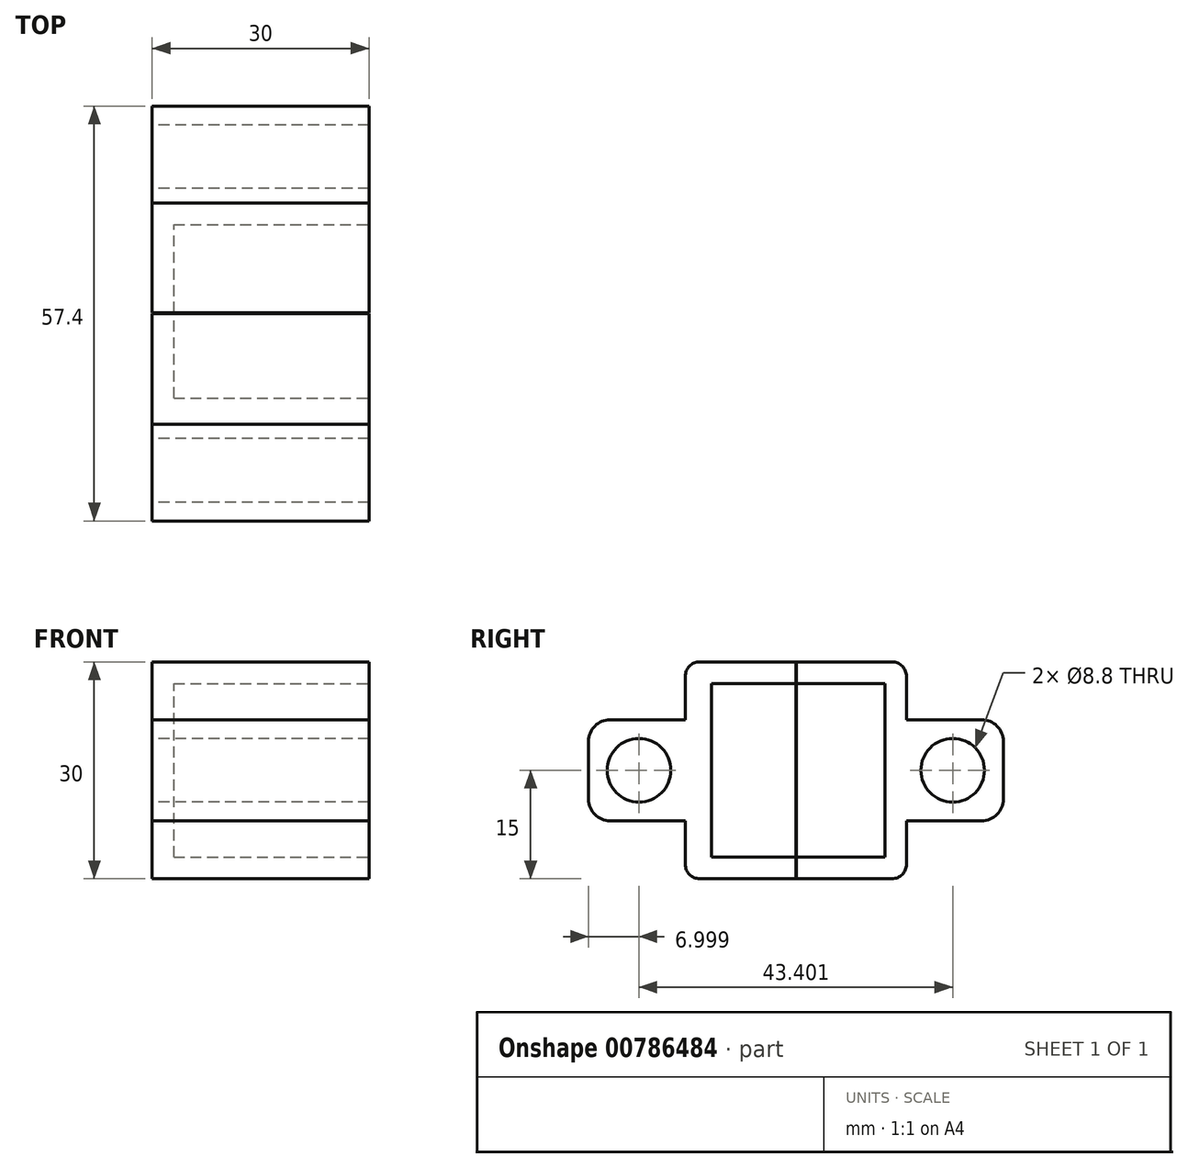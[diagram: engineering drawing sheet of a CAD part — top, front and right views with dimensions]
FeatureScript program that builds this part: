
annotation { "Feature Type Name" : "Feature", "Feature Type Description" : "" }
export const myFeature = defineFeature(function(context is Context, id is Id, definition is map)
    precondition{}
    {
        {
            var Q0;
            Q0=qCreatedBy(makeId("Top.planeOp"),FACE);
            var sketch = newSketch(context, id + "F0", { "sketchPlane" : qUnion([Q0])});
            skLineSegment(sketch, "E0.bottom", {"start": v(0, 15.3) * mm, "end": v(30, 15.3) * mm});
            skLineSegment(sketch, "E0.top", {"start": v(0, -14.7) * mm, "end": v(30, -14.7) * mm});
            skLineSegment(sketch, "E0.left", {"start": v(0, 15.3) * mm, "end": v(0, -14.7) * mm});
            skLineSegment(sketch, "E0.right", {"start": v(30, 15.3) * mm, "end": v(30, -14.7) * mm});
            skSolve(sketch);
        }
        {
            var Q0;
            Q0 = qSketchRegion(id + "F0", true);
            extrude(context, id + "F1", {"entities" : qUnion([Q0]), "depth" : 30 * mm, "offsetDistance" : 25 * mm});
        }
        {
            var Q0;
            Q0=makeQuery(id+"F1.opExtrude","SWEPT_FACE",FACE,{"disambiguationData":[OSD([sQuery(id+"F0.wireOp",EDGE,"E0.top")])]});
            var sketch = newSketch(context, id + "F2", { "sketchPlane" : qUnion([Q0])});
            skLineSegment(sketch, "E1.bottom", {"start": v(0, 8) * mm, "end": v(30, 8) * mm});
            skLineSegment(sketch, "E1.top", {"start": v(0, 22) * mm, "end": v(30, 22) * mm});
            skLineSegment(sketch, "E1.left", {"start": v(0, 8) * mm, "end": v(0, 22) * mm});
            skLineSegment(sketch, "E1.right", {"start": v(30, 8) * mm, "end": v(30, 22) * mm});
            skSolve(sketch);
        }
        {
            var Q0;
            Q0 = qSketchRegion(id + "F2", true);
            extrude(context, id + "F3", {"entities" : qUnion([Q0]), "operationType" : NewBodyOperationType.ADD, "depth" : 14 * mm, "offsetDistance" : 25 * mm});
        }
        {
            var Q0;
            Q0=makeQuery(id+"F3.boolean.opBoolean","MERGE",FACE,{"derivedFrom":[makeQuery(id+"F1.opExtrude","SWEPT_FACE",FACE,{"disambiguationData":[OSD([sQuery(id+"F0.wireOp",EDGE,"E0.left")])]}),makeQuery(id+"F3.opExtrude","SWEPT_FACE",FACE,{"disambiguationData":[OSD([sQuery(id+"F2.wireOp",EDGE,"E1.left")])]})]});
            var sketch = newSketch(context, id + "F4", { "sketchPlane" : qUnion([Q0])});
            skCircle(sketch, "E2", {"center": v(21.7, 15) * mm, "radius": 4.4 * mm});
            skPoint(sketch, "E2.centerSnap0", {"position": v(28.7, 15) * mm});
            skPoint(sketch, "E2.centerSnap1", {"position": v(21.7, 8) * mm});
            skSolve(sketch);
        }
        {
            var Q0;
            Q0 = qSketchRegion(id + "F4", true);
            extrude(context, id + "F5", {"entities" : qUnion([Q0]), "operationType" : NewBodyOperationType.REMOVE, "oppositeDirection" : true, "depth" : 30 * mm, "offsetDistance" : 25 * mm});
        }
        {
            var Q0;
            Q0=makeQuery(id+"F1.opExtrude","SWEPT_BODY",BODY,{"disambiguationData":[OSD([sQuery(id+"F0.wireOp",EDGE,"E0.bottom"),sQuery(id+"F0.wireOp",EDGE,"E0.top"),sQuery(id+"F0.wireOp",EDGE,"E0.left"),sQuery(id+"F0.wireOp",EDGE,"E0.right")])]});
            var Q1;
            Q1=qCreatedBy(makeId("Front.planeOp"),FACE);
            mirror(context, id + "F6", {"operationType" : NewBodyOperationType.ADD, "entities" : qUnion([Q0]), "mirrorPlane" : qUnion([Q1])});
        }
        {
            var Q0;
            Q0=makeQuery(id+"F3.opExtrude","CAP_EDGE",EDGE,{"disambiguationData":[OSD([sQuery(id+"F2.wireOp",EDGE,"E1.bottom")])],"isStart":false});
            var Q1;
            Q1=makeQuery(id+"F3.opExtrude","CAP_EDGE",EDGE,{"disambiguationData":[OSD([sQuery(id+"F2.wireOp",EDGE,"E1.top")])],"isStart":false});
            fillet(context, id + "F7", {"entities" : qUnion([Q0, Q1]), "radius" : 3 * mm, "tangentPropagation" : true, "allowEdgeOverflow" : false});
        }
        {
            var Q0;
            Q0=makeQuery(id+"F6.opPattern","COPY",EDGE,{"derivedFrom":makeQuery(id+"F3.opExtrude","CAP_EDGE",EDGE,{"disambiguationData":[OSD([sQuery(id+"F2.wireOp",EDGE,"E1.bottom")])],"isStart":false}),"instanceName":"1"});
            var Q1;
            Q1=makeQuery(id+"F6.opPattern","COPY",EDGE,{"derivedFrom":makeQuery(id+"F3.opExtrude","CAP_EDGE",EDGE,{"disambiguationData":[OSD([sQuery(id+"F2.wireOp",EDGE,"E1.top")])],"isStart":false}),"instanceName":"1"});
            fillet(context, id + "F8", {"entities" : qUnion([Q0, Q1]), "radius" : 3 * mm, "tangentPropagation" : true, "allowEdgeOverflow" : false});
        }
        {
            var Q0;
            {var subQ0=makeQuery(id+"F3.boolean.opBoolean","MERGE",FACE,{"derivedFrom":[makeQuery(id+"F1.opExtrude","SWEPT_FACE",FACE,{"disambiguationData":[OSD([sQuery(id+"F0.wireOp",EDGE,"E0.right")])]}),makeQuery(id+"F3.opExtrude","SWEPT_FACE",FACE,{"disambiguationData":[OSD([sQuery(id+"F2.wireOp",EDGE,"E1.right")])]})]});Q0=makeQuery(id+"F6.boolean.opBoolean","MERGE",FACE,{"derivedFrom":[subQ0,makeQuery(id+"F6.opPattern","COPY",FACE,{"derivedFrom":subQ0,"instanceName":"1"})]});}
            var sketch = newSketch(context, id + "F9", { "sketchPlane" : qUnion([Q0])});
            skLineSegment(sketch, "E3.bottom", {"start": v(-11.7, 27) * mm, "end": v(12.3, 27) * mm});
            skLineSegment(sketch, "E3.top", {"start": v(-11.7, 3) * mm, "end": v(12.3, 3) * mm});
            skLineSegment(sketch, "E3.left", {"start": v(-11.7, 27) * mm, "end": v(-11.7, 3) * mm});
            skLineSegment(sketch, "E3.right", {"start": v(12.3, 27) * mm, "end": v(12.3, 3) * mm});
            skSolve(sketch);
        }
        {
            var Q0;
            Q0 = qSketchRegion(id + "F9", true);
            extrude(context, id + "F10", {"entities" : qUnion([Q0]), "operationType" : NewBodyOperationType.REMOVE, "oppositeDirection" : true, "depth" : 27 * mm, "offsetDistance" : 25 * mm});
        }
        {
            var Q0;
            Q0=makeQuery(id+"F6.opPattern","COPY",EDGE,{"derivedFrom":makeQuery(id+"F1.opExtrude","CAP_EDGE",EDGE,{"disambiguationData":[OSD([sQuery(id+"F0.wireOp",EDGE,"E0.bottom")])],"isStart":true}),"instanceName":"1"});
            var Q1;
            Q1=makeQuery(id+"F6.opPattern","COPY",EDGE,{"derivedFrom":makeQuery(id+"F1.opExtrude","CAP_EDGE",EDGE,{"disambiguationData":[OSD([sQuery(id+"F0.wireOp",EDGE,"E0.bottom")])],"isStart":false}),"instanceName":"1"});
            var Q2;
            Q2=makeQuery(id+"F1.opExtrude","CAP_EDGE",EDGE,{"disambiguationData":[OSD([sQuery(id+"F0.wireOp",EDGE,"E0.bottom")])],"isStart":false});
            var Q3;
            Q3=makeQuery(id+"F1.opExtrude","CAP_EDGE",EDGE,{"disambiguationData":[OSD([sQuery(id+"F0.wireOp",EDGE,"E0.bottom")])],"isStart":true});
            fillet(context, id + "F11", {"entities" : qUnion([Q0, Q1, Q2, Q3]), "radius" : 2 * mm, "tangentPropagation" : true, "allowEdgeOverflow" : false});
        }
        {
            var Q0;
            {var subQ0=makeQuery(id+"F3.boolean.opBoolean","MERGE",FACE,{"derivedFrom":[makeQuery(id+"F1.opExtrude","SWEPT_FACE",FACE,{"disambiguationData":[OSD([sQuery(id+"F0.wireOp",EDGE,"E0.left")])]}),makeQuery(id+"F3.opExtrude","SWEPT_FACE",FACE,{"disambiguationData":[OSD([sQuery(id+"F2.wireOp",EDGE,"E1.left")])]})]});Q0=makeQuery(id+"F6.boolean.opBoolean","MERGE",FACE,{"derivedFrom":[subQ0,makeQuery(id+"F6.opPattern","COPY",FACE,{"derivedFrom":subQ0,"instanceName":"1"})]});}
            var sketch = newSketch(context, id + "F12", { "sketchPlane" : qUnion([Q0])});
            skLineSegment(sketch, "E4.bottom", {"start": v(0, 30) * mm, "end": v(-0.1, 30) * mm});
            skLineSegment(sketch, "E4.top", {"start": v(0, 0) * mm, "end": v(-0.1, 0) * mm});
            skLineSegment(sketch, "E4.left", {"start": v(0, 30) * mm, "end": v(0, 0) * mm});
            skLineSegment(sketch, "E4.right", {"start": v(-0.1, 30) * mm, "end": v(-0.1, 0) * mm});
            skSolve(sketch);
        }
        {
            var Q0;
            Q0 = qSketchRegion(id + "F12", true);
            extrude(context, id + "F13", {"entities" : qUnion([Q0]), "operationType" : NewBodyOperationType.REMOVE, "oppositeDirection" : true, "depth" : 30 * mm, "offsetDistance" : 25 * mm});
        }
    });
